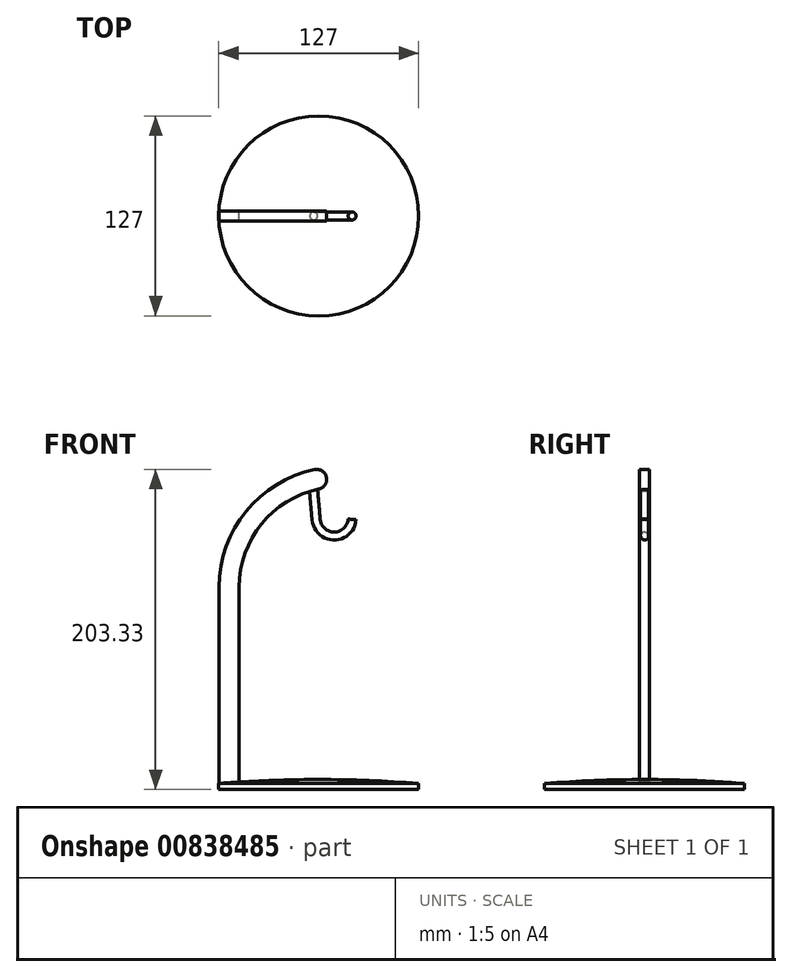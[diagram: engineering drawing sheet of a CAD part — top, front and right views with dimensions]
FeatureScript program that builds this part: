
annotation { "Feature Type Name" : "Feature", "Feature Type Description" : "" }
export const myFeature = defineFeature(function(context is Context, id is Id, definition is map)
    precondition{}
    {
        {
            var Q0;
            Q0=qCreatedBy(makeId("Right.planeOp"),FACE);
            var sketch = newSketch(context, id + "F0", { "sketchPlane" : qUnion([Q0])});
            skLineSegment(sketch, "E0", {"start": v(0, 0) * mm, "end": v(0, 6.35) * mm});
            skLineSegment(sketch, "E1", {"start": v(0, 0) * mm, "end": v(63.5, 0) * mm});
            skLineSegment(sketch, "E2", {"start": v(63.5, 0) * mm, "end": v(63.5, 3.8) * mm});
            skArc(sketch, "E3", {"start": v(63.5, 3.8) * mm, "mid": v(31.78, 5.71) * mm, "end": v(0, 6.35) * mm});
            skSolve(sketch);
        }
        {
            var Q0;
            Q0 = qSketchRegion(id + "F0", true);
            var Q1;
            Q1=sQuery(id+"F0.wireOp",EDGE,"E0");
            revolve(context, id + "F1", {"surfaceOperationType" : NewSurfaceOperationType.NEW, "entities" : qUnion([Q0]), "axis" : qUnion([Q1]), "revolveType" : RevolveType.FULL});
        }
        {
            var Q0;
            Q0=qCreatedBy(makeId("Front.planeOp"),FACE);
            var sketch = newSketch(context, id + "F2", { "sketchPlane" : qUnion([Q0])});
            skLineSegment(sketch, "E4", {"start": v(-50.55, 0) * mm, "end": v(-63.25, 0) * mm});
            skLineSegment(sketch, "E5", {"start": v(-63.25, 0) * mm, "end": v(-63.25, 128.6) * mm});
            skLineSegment(sketch, "E6", {"start": v(-50.55, 0) * mm, "end": v(-50.55, 128.6) * mm});
            skArc(sketch, "E7", {"start": v(-2.6, 203.2) * mm, "mid": v(-46.17, 176.67) * mm, "end": v(-63.25, 128.6) * mm});
            skArc(sketch, "E8", {"start": v(0, 190.77) * mm, "mid": v(-36.31, 168.66) * mm, "end": v(-50.55, 128.6) * mm});
            skArc(sketch, "E9", {"start": v(0, 190.77) * mm, "mid": v(4.92, 198.28) * mm, "end": v(-2.6, 203.2) * mm});
            skSolve(sketch);
        }
        {
            var Q0;
            Q0 = qSketchRegion(id + "F2", true);
            extrude(context, id + "F3", {"entities" : qUnion([Q0]), "operationType" : NewBodyOperationType.ADD, "endBound" : BoundingType.SYMMETRIC, "depth" : 6.35 * mm, "offsetDistance" : 25.4 * mm});
        }
        {
            var Q0;
            Q0=qCreatedBy(makeId("Front.planeOp"),FACE);
            var sketch = newSketch(context, id + "F4", { "sketchPlane" : qUnion([Q0])});
            skLineSegment(sketch, "E10", {"start": v(-1.3, 196.98) * mm, "end": v(0.92, 171.68) * mm});
            skArc(sketch, "E11", {"start": v(0.92, 171.68) * mm, "mid": v(9.82, 163.57) * mm, "end": v(18.64, 171.77) * mm});
            skPoint(sketch, "E12", {"position": v(-1.3, 196.98) * mm});
            skArc(sketch, "E13.0", {"start": v(-4.14, 171.24) * mm, "mid": v(9.9, 158.49) * mm, "end": v(23.71, 171.48) * mm});
            skLineSegment(sketch, "E13.1", {"start": v(-6.35, 196.47) * mm, "end": v(-4.14, 171.24) * mm});
            skLineSegment(sketch, "E14", {"start": v(18.64, 171.77) * mm, "end": v(23.71, 171.48) * mm});
            skLineSegment(sketch, "E15", {"start": v(-1.3, 196.98) * mm, "end": v(-6.35, 196.47) * mm});
            skLineSegment(sketch, "E16", {"start": v(0, 0) * mm, "end": v(0, 234.67) * mm, "construction": true});
            skSolve(sketch);
        }
        {
            var Q0;
            Q0 = qSketchRegion(id + "F4", true);
            extrude(context, id + "F5", {"entities" : qUnion([Q0]), "operationType" : NewBodyOperationType.ADD, "endBound" : BoundingType.SYMMETRIC, "depth" : 5.08 * mm, "offsetDistance" : 25.4 * mm});
        }
        {
            var Q0;
            Q0=makeQuery(id+"F5.opExtrude","CAP_EDGE",EDGE,{"disambiguationData":[OSD([sQuery(id+"F4.wireOp",EDGE,"E10")])],"isStart":false});
            var Q1;
            Q1=makeQuery(id+"F5.opExtrude","CAP_EDGE",EDGE,{"disambiguationData":[OSD([sQuery(id+"F4.wireOp",EDGE,"E10")])],"isStart":true});
            var Q2;
            Q2=makeQuery(id+"F5.opExtrude","CAP_EDGE",EDGE,{"disambiguationData":[OSD([sQuery(id+"F4.wireOp",EDGE,"E11")])],"isStart":false});
            var Q3;
            Q3=makeQuery(id+"F5.opExtrude","CAP_EDGE",EDGE,{"disambiguationData":[OSD([sQuery(id+"F4.wireOp",EDGE,"E13.0")])],"isStart":false});
            var Q4;
            Q4=makeQuery(id+"F5.opExtrude","CAP_EDGE",EDGE,{"disambiguationData":[OSD([sQuery(id+"F4.wireOp",EDGE,"E13.1")])],"isStart":false});
            var Q5;
            Q5=makeQuery(id+"F5.opExtrude","CAP_EDGE",EDGE,{"disambiguationData":[OSD([sQuery(id+"F4.wireOp",EDGE,"E13.0")])],"isStart":true});
            var Q6;
            Q6=makeQuery(id+"F5.opExtrude","CAP_EDGE",EDGE,{"disambiguationData":[OSD([sQuery(id+"F4.wireOp",EDGE,"E13.1")])],"isStart":true});
            var Q7;
            Q7=makeQuery(id+"F5.opExtrude","CAP_EDGE",EDGE,{"disambiguationData":[OSD([sQuery(id+"F4.wireOp",EDGE,"E11")])],"isStart":true});
            fillet(context, id + "F6", {"entities" : qUnion([Q0, Q1, Q2, Q3, Q4, Q5, Q6, Q7]), "radius" : 2.54 * mm, "tangentPropagation" : true, "allowEdgeOverflow" : false});
        }
    });
